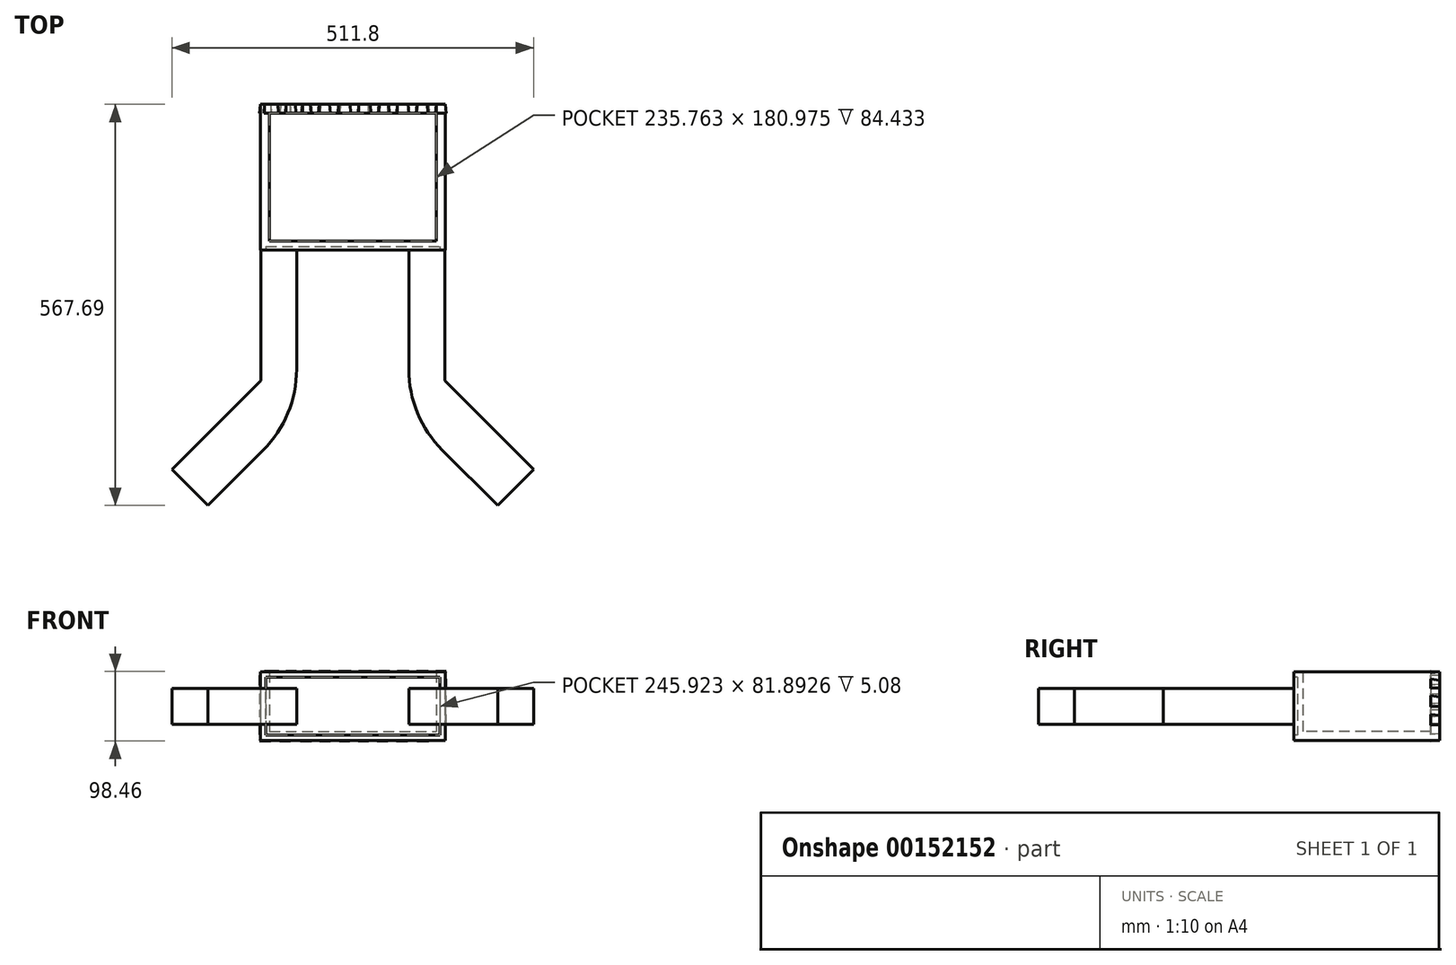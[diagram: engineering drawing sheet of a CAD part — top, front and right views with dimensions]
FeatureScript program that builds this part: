
annotation { "Feature Type Name" : "Feature", "Feature Type Description" : "" }
export const myFeature = defineFeature(function(context is Context, id is Id, definition is map)
    precondition{}
    {
        {
            var Q0;
            Q0=qCreatedBy(makeId("Front.planeOp"),FACE);
            var sketch = newSketch(context, id + "F0", { "sketchPlane" : qUnion([Q0])});
            skLineSegment(sketch, "E0.bottom", {"start": v(-79.66, 25.4) * mm, "end": v(-130.46, 25.4) * mm});
            skLineSegment(sketch, "E0.top", {"start": v(-79.66, -25.4) * mm, "end": v(-130.46, -25.4) * mm});
            skLineSegment(sketch, "E0.left", {"start": v(-79.66, 25.4) * mm, "end": v(-79.66, -25.4) * mm});
            skLineSegment(sketch, "E0.right", {"start": v(-130.46, 25.4) * mm, "end": v(-130.46, -25.4) * mm});
            skPoint(sketch, "E0.middle", {"position": v(-105.06, 0) * mm});
            skLineSegment(sketch, "E1.bottom", {"start": v(129.89, 25.4) * mm, "end": v(79.09, 25.4) * mm});
            skLineSegment(sketch, "E1.top", {"start": v(129.89, -25.4) * mm, "end": v(79.09, -25.4) * mm});
            skLineSegment(sketch, "E1.left", {"start": v(129.89, 25.4) * mm, "end": v(129.89, -25.4) * mm});
            skLineSegment(sketch, "E1.right", {"start": v(79.09, 25.4) * mm, "end": v(79.09, -25.4) * mm});
            skPoint(sketch, "E1.middle", {"position": v(104.49, 0) * mm});
            skSolve(sketch);
        }
        {
            var Q0;
            Q0=makeQuery(id+"F0.imprint","IMPRINT",FACE,{"disambiguationData":[TD([[makeQuery(id+"F0.imprint","IMPRINT",EDGE,{"derivedFrom":sQuery(id+"F0.wireOp",EDGE,"E0.bottom")}),1.0]])]});
            var Q1;
            Q1=makeQuery(id+"F0.imprint","IMPRINT",FACE,{"disambiguationData":[TD([[makeQuery(id+"F0.imprint","IMPRINT",EDGE,{"derivedFrom":sQuery(id+"F0.wireOp",EDGE,"E1.bottom")}),1.0]])]});
            extrude(context, id + "F1", {"entities" : qUnion([Q0, Q1]), "depth" : 235.58 * mm});
        }
        {
            var Q0;
            Q0=makeQuery(id+"F1.opExtrude","CAP_EDGE",EDGE,{"disambiguationData":[OSD([sQuery(id+"F0.wireOp",EDGE,"E1.left")])],"isStart":false});
            chamfer(context, id + "F2", {"entities" : qUnion([Q0]), "width" : 50.8 * mm, "tangentPropagation" : true});
        }
        {
            var Q0;
            Q0=makeQuery(id+"F1.opExtrude","CAP_EDGE",EDGE,{"disambiguationData":[OSD([sQuery(id+"F0.wireOp",EDGE,"E0.right")])],"isStart":false});
            chamfer(context, id + "F3", {"entities" : qUnion([Q0]), "width" : 50.8 * mm, "tangentPropagation" : true});
        }
        {
            var Q0;
            Q0=makeQuery(id+"F3.opChamfer","BLEND_FACE",FACE,{"disambiguationData":[OSD([sQuery(id+"F0.wireOp",EDGE,"E0.right")])]});
            var sketch = newSketch(context, id + "F4", { "sketchPlane" : qUnion([Q0])});
            skLineSegment(sketch, "E2.bottom", {"start": v(38.41, 25.4) * mm, "end": v(110.25, 25.4) * mm});
            skLineSegment(sketch, "E2.top", {"start": v(38.41, -25.4) * mm, "end": v(110.25, -25.4) * mm});
            skLineSegment(sketch, "E2.left", {"start": v(38.41, 25.4) * mm, "end": v(38.41, -25.4) * mm});
            skLineSegment(sketch, "E2.right", {"start": v(110.25, 25.4) * mm, "end": v(110.25, -25.4) * mm});
            skSolve(sketch);
        }
        {
            var Q0;
            Q0=makeQuery(id+"F2.opChamfer","BLEND_FACE",FACE,{"disambiguationData":[OSD([sQuery(id+"F0.wireOp",EDGE,"E1.left")])]});
            var sketch = newSketch(context, id + "F5", { "sketchPlane" : qUnion([Q0])});
            skLineSegment(sketch, "E3.bottom", {"start": v(-110.66, 25.4) * mm, "end": v(-38.82, 25.4) * mm});
            skLineSegment(sketch, "E3.top", {"start": v(-110.66, -25.4) * mm, "end": v(-38.82, -25.4) * mm});
            skLineSegment(sketch, "E3.left", {"start": v(-110.66, 25.4) * mm, "end": v(-110.66, -25.4) * mm});
            skLineSegment(sketch, "E3.right", {"start": v(-38.82, 25.4) * mm, "end": v(-38.82, -25.4) * mm});
            skSolve(sketch);
        }
        {
            var Q0;
            Q0=makeQuery(id+"F4.imprint","IMPRINT",FACE,{"disambiguationData":[TD([[makeQuery(id+"F4.imprint","IMPRINT",EDGE,{"derivedFrom":sQuery(id+"F4.wireOp",EDGE,"E2.bottom")}),-1.0]])]});
            extrude(context, id + "F6", {"entities" : qUnion([Q0]), "operationType" : NewBodyOperationType.ADD, "depth" : 177.8 * mm});
        }
        {
            var Q0;
            Q0=makeQuery(id+"F5.imprint","IMPRINT",FACE,{"disambiguationData":[TD([[makeQuery(id+"F5.imprint","IMPRINT",EDGE,{"derivedFrom":sQuery(id+"F5.wireOp",EDGE,"E3.bottom")}),-1.0]])]});
            extrude(context, id + "F7", {"entities" : qUnion([Q0]), "operationType" : NewBodyOperationType.ADD, "depth" : 177.8 * mm});
        }
        {
            var Q0;
            Q0=makeQuery(id+"F7.boolean.opBoolean","MERGE",EDGE,{"derivedFrom":[makeQuery(id+"F2.opChamfer","BLEND_EDGE",EDGE,{"blendedFrom":[makeQuery(id+"F1.opExtrude","CAP_EDGE",EDGE,{"disambiguationData":[OSD([sQuery(id+"F0.wireOp",EDGE,"E1.left")])],"isStart":false}),makeQuery(id+"F1.opExtrude","SWEPT_FACE",FACE,{"disambiguationData":[OSD([sQuery(id+"F0.wireOp",EDGE,"E1.right")])]})],"blendedInto":[makeQuery(id+"F1.opExtrude","SWEPT_FACE",FACE,{"disambiguationData":[OSD([sQuery(id+"F0.wireOp",EDGE,"E1.right")])]})]}),makeQuery(id+"F7.opExtrude","CAP_EDGE",EDGE,{"disambiguationData":[OSD([sQuery(id+"F5.wireOp",EDGE,"E3.left")])],"isStart":true})]});
            var Q1;
            Q1=makeQuery(id+"F6.boolean.opBoolean","MERGE",EDGE,{"derivedFrom":[makeQuery(id+"F3.opChamfer","BLEND_EDGE",EDGE,{"blendedFrom":[makeQuery(id+"F1.opExtrude","CAP_EDGE",EDGE,{"disambiguationData":[OSD([sQuery(id+"F0.wireOp",EDGE,"E0.right")])],"isStart":false}),makeQuery(id+"F1.opExtrude","SWEPT_FACE",FACE,{"disambiguationData":[OSD([sQuery(id+"F0.wireOp",EDGE,"E0.left")])]})],"blendedInto":[makeQuery(id+"F1.opExtrude","SWEPT_FACE",FACE,{"disambiguationData":[OSD([sQuery(id+"F0.wireOp",EDGE,"E0.left")])]})]}),makeQuery(id+"F6.opExtrude","CAP_EDGE",EDGE,{"disambiguationData":[OSD([sQuery(id+"F4.wireOp",EDGE,"E2.right")])],"isStart":true})]});
            fillet(context, id + "F8", {"entities" : qUnion([Q0, Q1]), "radius" : 161.85 * mm, "tangentPropagation" : true, "allowEdgeOverflow" : false});
        }
        {
            var Q0;
            Q0=qCreatedBy(makeId("Front.planeOp"),FACE);
            var sketch = newSketch(context, id + "F9", { "sketchPlane" : qUnion([Q0])});
            skLineSegment(sketch, "E4.bottom", {"start": v(-130.58, 48.57) * mm, "end": v(130.58, 48.57) * mm});
            skLineSegment(sketch, "E4.top", {"start": v(-130.58, -48.57) * mm, "end": v(130.58, -48.57) * mm});
            skLineSegment(sketch, "E4.left", {"start": v(-130.58, 48.57) * mm, "end": v(-130.58, -48.57) * mm});
            skLineSegment(sketch, "E4.right", {"start": v(130.58, 48.57) * mm, "end": v(130.58, -48.57) * mm});
            skPoint(sketch, "E4.middle", {"position": v(0, 0) * mm});
            skSolve(sketch);
        }
        {
            var Q0;
            Q0=makeQuery(id+"F9.imprint","IMPRINT",FACE,{"disambiguationData":[TD([[makeQuery(id+"F9.imprint","IMPRINT",EDGE,{"derivedFrom":sQuery(id+"F9.wireOp",EDGE,"E4.bottom")}),-1.0]])]});
            extrude(context, id + "F10", {"entities" : qUnion([Q0]), "oppositeDirection" : true, "depth" : 206.38 * mm});
        }
        {
            var Q0;
            Q0=makeQuery(id+"F10.opExtrude","SWEPT_FACE",FACE,{"disambiguationData":[OSD([sQuery(id+"F9.wireOp",EDGE,"E4.bottom")])]});
            shell(context, id + "F11", {"entities" : qUnion([Q0]), "thickness" : 12.7 * mm});
        }
        {
            var Q0;
            Q0=makeQuery(id+"F10.opExtrude","CAP_FACE",FACE,{"disambiguationData":[OSD([sQuery(id+"F9.wireOp",EDGE,"E4.bottom"),sQuery(id+"F9.wireOp",EDGE,"E4.top"),sQuery(id+"F9.wireOp",EDGE,"E4.left"),sQuery(id+"F9.wireOp",EDGE,"E4.right")])],"isStart":true});
            shell(context, id + "F12", {"entities" : qUnion([Q0]), "thickness" : 7.62 * mm});
        }
        {
            var Q0;
            Q0=makeQuery(id+"F10.opExtrude","CAP_FACE",FACE,{"disambiguationData":[OSD([sQuery(id+"F9.wireOp",EDGE,"E4.bottom"),sQuery(id+"F9.wireOp",EDGE,"E4.top"),sQuery(id+"F9.wireOp",EDGE,"E4.left"),sQuery(id+"F9.wireOp",EDGE,"E4.right")])],"isStart":false});
            var sketch = newSketch(context, id + "F13", { "sketchPlane" : qUnion([Q0])});
            skLineSegment(sketch, "E5", {"start": v(-130.58, -25.84) * mm, "end": v(-107.14, -48.57) * mm});
            skLineSegment(sketch, "E6", {"start": v(-107.14, -48.57) * mm, "end": v(-92.3, -48.57) * mm});
            skLineSegment(sketch, "E7", {"start": v(-92.3, -48.57) * mm, "end": v(-130.58, -12.76) * mm});
            skLineSegment(sketch, "E8", {"start": v(-130.58, -12.76) * mm, "end": v(-130.58, 0) * mm});
            skLineSegment(sketch, "E9", {"start": v(-130.58, 0) * mm, "end": v(-77.1, -48.57) * mm});
            skLineSegment(sketch, "E10", {"start": v(-77.1, -48.57) * mm, "end": v(-62.96, -48.57) * mm});
            skLineSegment(sketch, "E11", {"start": v(-62.96, -48.57) * mm, "end": v(-130.58, 13.4) * mm});
            skLineSegment(sketch, "E12", {"start": v(-130.58, 13.4) * mm, "end": v(-130.58, 26.11) * mm});
            skLineSegment(sketch, "E13", {"start": v(-130.58, 26.11) * mm, "end": v(-48.83, -48.57) * mm});
            skLineSegment(sketch, "E14", {"start": v(-48.83, -48.57) * mm, "end": v(-36.1, -48.57) * mm});
            skLineSegment(sketch, "E15", {"start": v(-36.1, -48.57) * mm, "end": v(-130.58, 37.07) * mm});
            skLineSegment(sketch, "E16", {"start": v(-130.58, 37.07) * mm, "end": v(-130.58, 48.57) * mm});
            skLineSegment(sketch, "E17", {"start": v(-130.58, 48.57) * mm, "end": v(-21.61, -48.57) * mm});
            skLineSegment(sketch, "E18", {"start": v(-21.61, -48.57) * mm, "end": v(-9.24, -48.57) * mm});
            skLineSegment(sketch, "E19", {"start": v(-9.24, -48.57) * mm, "end": v(-118.1, 48.57) * mm});
            skLineSegment(sketch, "E20", {"start": v(-118.1, 48.57) * mm, "end": v(-104.67, 48.57) * mm});
            skLineSegment(sketch, "E21", {"start": v(-104.67, 48.57) * mm, "end": v(4.9, -48.57) * mm});
            skLineSegment(sketch, "E22", {"start": v(4.9, -48.57) * mm, "end": v(17.26, -48.57) * mm});
            skLineSegment(sketch, "E23", {"start": v(17.26, -48.57) * mm, "end": v(-90.53, 48.57) * mm});
            skLineSegment(sketch, "E24", {"start": v(-90.53, 48.57) * mm, "end": v(-77.8, 48.57) * mm});
            skLineSegment(sketch, "E25", {"start": v(-77.8, 48.57) * mm, "end": v(32.46, -48.57) * mm});
            skLineSegment(sketch, "E26", {"start": v(32.46, -48.57) * mm, "end": v(45.18, -48.57) * mm});
            skLineSegment(sketch, "E27", {"start": v(45.18, -48.57) * mm, "end": v(-62.96, 48.57) * mm});
            skLineSegment(sketch, "E28", {"start": v(-62.96, 48.57) * mm, "end": v(-50.24, 48.57) * mm});
            skLineSegment(sketch, "E29", {"start": v(-50.24, 48.57) * mm, "end": v(58.97, -48.57) * mm});
            skLineSegment(sketch, "E30", {"start": v(58.97, -48.57) * mm, "end": v(72.4, -48.57) * mm});
            skLineSegment(sketch, "E31", {"start": v(72.4, -48.57) * mm, "end": v(-37.16, 48.57) * mm});
            skLineSegment(sketch, "E32", {"start": v(-37.16, 48.57) * mm, "end": v(-24.09, 48.57) * mm});
            skLineSegment(sketch, "E33", {"start": v(-24.09, 48.57) * mm, "end": v(89, -48.57) * mm});
            skLineSegment(sketch, "E34", {"start": v(89, -48.57) * mm, "end": v(101.96, -48.57) * mm});
            skLineSegment(sketch, "E35", {"start": v(101.96, -48.57) * mm, "end": v(-8.5, 48.57) * mm});
            skLineSegment(sketch, "E36", {"start": v(-8.5, 48.57) * mm, "end": v(4.6, 48.57) * mm});
            skLineSegment(sketch, "E37", {"start": v(4.6, 48.57) * mm, "end": v(116.33, -48.57) * mm});
            skLineSegment(sketch, "E38", {"start": v(116.33, -48.57) * mm, "end": v(130.58, -48.57) * mm});
            skLineSegment(sketch, "E39", {"start": v(130.58, -48.57) * mm, "end": v(20.24, 48.57) * mm});
            skLineSegment(sketch, "E40", {"start": v(20.24, 48.57) * mm, "end": v(33.36, 48.57) * mm});
            skLineSegment(sketch, "E41", {"start": v(33.36, 48.57) * mm, "end": v(130.58, -38.45) * mm});
            skLineSegment(sketch, "E42", {"start": v(130.58, -38.45) * mm, "end": v(130.58, -24.83) * mm});
            skLineSegment(sketch, "E43", {"start": v(130.58, -24.83) * mm, "end": v(47.73, 48.57) * mm});
            skLineSegment(sketch, "E44", {"start": v(47.73, 48.57) * mm, "end": v(60.6, 48.57) * mm});
            skLineSegment(sketch, "E45", {"start": v(60.6, 48.57) * mm, "end": v(130.58, -13.99) * mm});
            skLineSegment(sketch, "E46", {"start": v(130.58, -13.99) * mm, "end": v(130.58, -5.41) * mm});
            skLineSegment(sketch, "E47", {"start": v(130.58, -5.41) * mm, "end": v(70.94, 48.57) * mm});
            skLineSegment(sketch, "E48", {"start": v(70.94, 48.57) * mm, "end": v(82.03, 48.57) * mm});
            skLineSegment(sketch, "E49", {"start": v(82.03, 48.57) * mm, "end": v(130.58, 4.67) * mm});
            skLineSegment(sketch, "E50", {"start": v(130.58, 4.67) * mm, "end": v(130.58, 17.28) * mm});
            skLineSegment(sketch, "E51", {"start": v(130.58, 17.28) * mm, "end": v(94.4, 48.57) * mm});
            skLineSegment(sketch, "E52", {"start": v(94.4, 48.57) * mm, "end": v(107, 48.57) * mm});
            skLineSegment(sketch, "E53", {"start": v(107, 48.57) * mm, "end": v(130.58, 31.16) * mm});
            skLineSegment(sketch, "E54", {"start": v(130.58, 31.16) * mm, "end": v(130.58, 43.77) * mm});
            skLineSegment(sketch, "E55", {"start": v(130.58, 43.77) * mm, "end": v(124.9, 48.57) * mm});
            skSolve(sketch);
        }
        {
            var Q0;
            {var subQ0=sQuery(id+"F13.wireOp",EDGE,"E5");Q0=makeQuery(id+"F13.imprint","IMPRINT",FACE,{"disambiguationData":[TD([[makeQuery(id+"F13.imprint","IMPRINT",EDGE,{"derivedFrom":subQ0}),1.0]])]});}
            var Q1;
            {var subQ0=sQuery(id+"F13.wireOp",EDGE,"E9");Q1=makeQuery(id+"F13.imprint","IMPRINT",FACE,{"disambiguationData":[TD([[makeQuery(id+"F13.imprint","IMPRINT",EDGE,{"derivedFrom":subQ0}),1.0]])]});}
            var Q2;
            {var subQ0=sQuery(id+"F13.wireOp",EDGE,"E13");Q2=makeQuery(id+"F13.imprint","IMPRINT",FACE,{"disambiguationData":[TD([[makeQuery(id+"F13.imprint","IMPRINT",EDGE,{"derivedFrom":subQ0}),1.0]])]});}
            var Q3;
            {var subQ0=sQuery(id+"F13.wireOp",EDGE,"E17");Q3=makeQuery(id+"F13.imprint","IMPRINT",FACE,{"disambiguationData":[TD([[makeQuery(id+"F13.imprint","IMPRINT",EDGE,{"derivedFrom":subQ0}),1.0]])]});}
            var Q4;
            {var subQ0=sQuery(id+"F13.wireOp",EDGE,"E21");Q4=makeQuery(id+"F13.imprint","IMPRINT",FACE,{"disambiguationData":[TD([[makeQuery(id+"F13.imprint","IMPRINT",EDGE,{"derivedFrom":subQ0}),1.0]])]});}
            var Q5;
            {var subQ0=sQuery(id+"F13.wireOp",EDGE,"E25");Q5=makeQuery(id+"F13.imprint","IMPRINT",FACE,{"disambiguationData":[TD([[makeQuery(id+"F13.imprint","IMPRINT",EDGE,{"derivedFrom":subQ0}),1.0]])]});}
            var Q6;
            {var subQ0=sQuery(id+"F13.wireOp",EDGE,"E29");Q6=makeQuery(id+"F13.imprint","IMPRINT",FACE,{"disambiguationData":[TD([[makeQuery(id+"F13.imprint","IMPRINT",EDGE,{"derivedFrom":subQ0}),1.0]])]});}
            var Q7;
            {var subQ0=sQuery(id+"F13.wireOp",EDGE,"E33");Q7=makeQuery(id+"F13.imprint","IMPRINT",FACE,{"disambiguationData":[TD([[makeQuery(id+"F13.imprint","IMPRINT",EDGE,{"derivedFrom":subQ0}),1.0]])]});}
            var Q8;
            {var subQ0=sQuery(id+"F13.wireOp",EDGE,"E37");Q8=makeQuery(id+"F13.imprint","IMPRINT",FACE,{"disambiguationData":[TD([[makeQuery(id+"F13.imprint","IMPRINT",EDGE,{"derivedFrom":subQ0}),1.0]])]});}
            var Q9;
            {var subQ0=sQuery(id+"F13.wireOp",EDGE,"E41");Q9=makeQuery(id+"F13.imprint","IMPRINT",FACE,{"disambiguationData":[TD([[makeQuery(id+"F13.imprint","IMPRINT",EDGE,{"derivedFrom":subQ0}),1.0]])]});}
            var Q10;
            {var subQ0=sQuery(id+"F13.wireOp",EDGE,"E45");Q10=makeQuery(id+"F13.imprint","IMPRINT",FACE,{"disambiguationData":[TD([[makeQuery(id+"F13.imprint","IMPRINT",EDGE,{"derivedFrom":subQ0}),1.0]])]});}
            var Q11;
            {var subQ0=sQuery(id+"F13.wireOp",EDGE,"E49");Q11=makeQuery(id+"F13.imprint","IMPRINT",FACE,{"disambiguationData":[TD([[makeQuery(id+"F13.imprint","IMPRINT",EDGE,{"derivedFrom":subQ0}),1.0]])]});}
            var Q12;
            {var subQ0=sQuery(id+"F13.wireOp",EDGE,"E53");Q12=makeQuery(id+"F13.imprint","IMPRINT",FACE,{"disambiguationData":[TD([[makeQuery(id+"F13.imprint","IMPRINT",EDGE,{"derivedFrom":subQ0}),1.0]])]});}
            extrude(context, id + "F14", {"entities" : qUnion([Q0, Q1, Q2, Q3, Q4, Q5, Q6, Q7, Q8, Q9, Q10, Q11, Q12]), "operationType" : NewBodyOperationType.ADD, "oppositeDirection" : true, "depth" : 12.7 * mm, "hasDraft" : true, "draftAngle" : 3 * degree});
        }
    });
